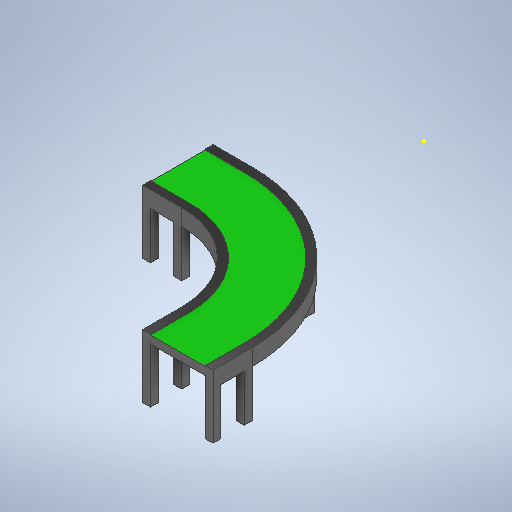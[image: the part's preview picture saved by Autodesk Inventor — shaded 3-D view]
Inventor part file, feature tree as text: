
AUTODESK INVENTOR PART (.ipt)
format: ipt  version: 2025.2 (Build 292293000, 293)  size: 418,816 bytes
history: native  units: mm
features: sketch x10, extrude x9, projected_geometry x3
ambient origin geometry x8: Origin, YZ Plane, XZ Plane, XY Plane, X Axis, Y Axis, Z Axis, Center Point
bodies: Solid1 (feature_tree)
feature tree (22):
  extrude  "Extrusion1"  Depth=2500.0mm TaperAngle=0.0deg
  extrude  "Extrusion2"  Depth=1100.0mm
  extrude  "Extrusion3"  Depth=600.0mm TaperAngle=0.0deg
  extrude  "Extrusion4"  Depth=600.0mm
  extrude  "Extrusion5"  Depth=290.0mm TaperAngle=0.0deg
  extrude  "Extrusion6"  Depth=100.0mm
  extrude  "Extrusion7"  TaperAngle=0.0deg  [1 undecoded]
  extrude  "Extrusion8"  Depth=100.0mm
  extrude  "Extrusion9"  TaperAngle=0.0deg  [1 undecoded]
  sketch  "Sketch10"  dims[d45=0.0mm d46=0.0mm]
  sketch  "Sketch1"  dims[d15=1100.0mm d16=0.0mm d21=2500.0mm d22=0.0mm]
  sketch  "Sketch2"  dims[d23=200.0mm d24=0.0mm d25=1100.0mm]
  projected_geometry  "Projected Loop1"
  sketch  "Sketch3"  dims[d26=600.0mm d27=3000.0mm d28=0.0mm]
  projected_geometry  "Projected Loop2"
  projected_geometry  "Projected Loop3"
  sketch  "Sketch4"  dims[d29=1100.0mm d30=600.0mm]
  sketch  "Sketch5"  dims[d31=3000.0mm d32=0.0mm d33=290.0mm d34=0.0mm]
  sketch  "Sketch6"  dims[d35=100.0mm d36=100.0mm]
  sketch  "Sketch7"  dims[d37=600.0mm d38=0.0mm d39=0.0mm]
  sketch  "Sketch8"  dims[d40=100.0mm d41=100.0mm]
  sketch  "Sketch9"  dims[d42=600.0mm d43=0.0mm d44=0.0mm]
note: 2 required parameter values undecoded (feature->parameter linkage not recoverable at this tier; creation-order binding heuristic only, values carry confidence <= 0.55)
